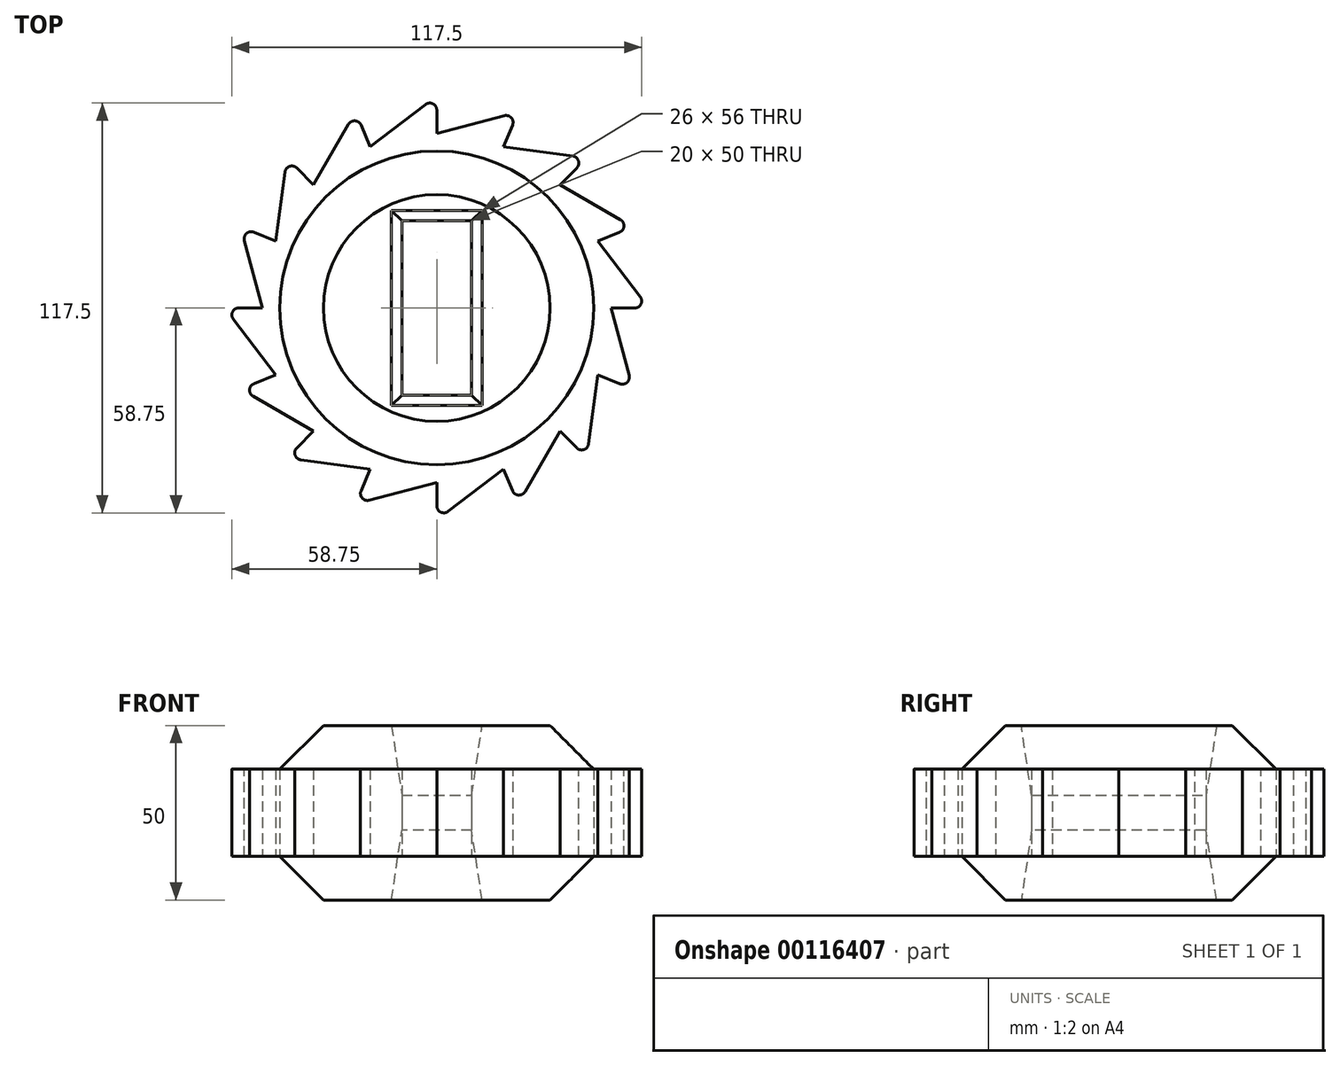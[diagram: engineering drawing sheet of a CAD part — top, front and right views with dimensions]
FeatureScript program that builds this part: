
annotation { "Feature Type Name" : "Feature", "Feature Type Description" : "" }
export const myFeature = defineFeature(function(context is Context, id is Id, definition is map)
    precondition{}
    {
        {
            var Q0;
            Q0=qCreatedBy(makeId("Top.planeOp"),FACE);
            var sketch = newSketch(context, id + "F0", { "sketchPlane" : qUnion([Q0])});
            skCircle(sketch, "E0.cCircle", {"center": v(0, 0) * mm, "radius": 50 * mm, "construction": true});
            skLineSegment(sketch, "E0.0", {"start": v(50, 0) * mm, "end": v(46.2, -19.13) * mm});
            skLineSegment(sketch, "E0.1", {"start": v(46.2, -19.13) * mm, "end": v(35.36, -35.36) * mm});
            skLineSegment(sketch, "E0.2", {"start": v(35.36, -35.36) * mm, "end": v(19.13, -46.2) * mm});
            skLineSegment(sketch, "E0.3", {"start": v(19.13, -46.2) * mm, "end": v(0, -50) * mm});
            skLineSegment(sketch, "E0.4", {"start": v(0, -50) * mm, "end": v(-19.13, -46.2) * mm});
            skLineSegment(sketch, "E0.5", {"start": v(-19.13, -46.2) * mm, "end": v(-35.36, -35.36) * mm});
            skLineSegment(sketch, "E0.6", {"start": v(-35.36, -35.36) * mm, "end": v(-46.2, -19.13) * mm});
            skLineSegment(sketch, "E0.7", {"start": v(-46.2, -19.13) * mm, "end": v(-50, 0) * mm});
            skLineSegment(sketch, "E0.8", {"start": v(-50, 0) * mm, "end": v(-46.2, 19.13) * mm});
            skLineSegment(sketch, "E0.9", {"start": v(-46.2, 19.13) * mm, "end": v(-35.36, 35.36) * mm});
            skLineSegment(sketch, "E0.10", {"start": v(-35.36, 35.36) * mm, "end": v(-19.13, 46.2) * mm});
            skLineSegment(sketch, "E0.11", {"start": v(-19.13, 46.2) * mm, "end": v(0, 50) * mm});
            skLineSegment(sketch, "E0.12", {"start": v(0, 50) * mm, "end": v(19.13, 46.2) * mm});
            skLineSegment(sketch, "E0.13", {"start": v(19.13, 46.2) * mm, "end": v(35.36, 35.36) * mm});
            skLineSegment(sketch, "E0.14", {"start": v(35.36, 35.36) * mm, "end": v(46.2, 19.13) * mm});
            skLineSegment(sketch, "E0.15", {"start": v(46.2, 19.13) * mm, "end": v(50, 0) * mm});
            skLineSegment(sketch, "E1", {"start": v(0, 60.8) * mm, "end": v(0, 50) * mm});
            skLineSegment(sketch, "E2", {"start": v(0, 60.8) * mm, "end": v(-19.13, 46.2) * mm});
            skLineSegment(sketch, "E3.1.0", {"start": v(-23.27, 56.17) * mm, "end": v(-35.36, 35.36) * mm});
            skLineSegment(sketch, "E3.1.1", {"start": v(-23.27, 56.17) * mm, "end": v(-19.13, 46.2) * mm});
            skLineSegment(sketch, "E3.2.0", {"start": v(-42.99, 42.99) * mm, "end": v(-46.2, 19.13) * mm});
            skLineSegment(sketch, "E3.2.1", {"start": v(-42.99, 42.99) * mm, "end": v(-35.36, 35.36) * mm});
            skLineSegment(sketch, "E3.3.0", {"start": v(-56.17, 23.27) * mm, "end": v(-50, 0) * mm});
            skLineSegment(sketch, "E3.3.1", {"start": v(-56.17, 23.27) * mm, "end": v(-46.2, 19.13) * mm});
            skLineSegment(sketch, "E3.4.0", {"start": v(-60.8, 0) * mm, "end": v(-46.2, -19.13) * mm});
            skLineSegment(sketch, "E3.4.1", {"start": v(-60.8, 0) * mm, "end": v(-50, 0) * mm});
            skLineSegment(sketch, "E3.5.0", {"start": v(-56.17, -23.27) * mm, "end": v(-35.36, -35.36) * mm});
            skLineSegment(sketch, "E3.5.1", {"start": v(-56.17, -23.27) * mm, "end": v(-46.2, -19.13) * mm});
            skLineSegment(sketch, "E3.6.0", {"start": v(-42.99, -42.99) * mm, "end": v(-19.13, -46.2) * mm});
            skLineSegment(sketch, "E3.6.1", {"start": v(-42.99, -42.99) * mm, "end": v(-35.36, -35.36) * mm});
            skLineSegment(sketch, "E3.7.0", {"start": v(-23.27, -56.17) * mm, "end": v(0, -50) * mm});
            skLineSegment(sketch, "E3.7.1", {"start": v(-23.27, -56.17) * mm, "end": v(-19.13, -46.2) * mm});
            skLineSegment(sketch, "E3.8.0", {"start": v(0, -60.8) * mm, "end": v(19.13, -46.2) * mm});
            skLineSegment(sketch, "E3.8.1", {"start": v(0, -60.8) * mm, "end": v(0, -50) * mm});
            skLineSegment(sketch, "E3.9.0", {"start": v(23.27, -56.17) * mm, "end": v(35.36, -35.36) * mm});
            skLineSegment(sketch, "E3.9.1", {"start": v(23.27, -56.17) * mm, "end": v(19.13, -46.2) * mm});
            skLineSegment(sketch, "E3.10.0", {"start": v(42.99, -42.99) * mm, "end": v(46.2, -19.13) * mm});
            skLineSegment(sketch, "E3.10.1", {"start": v(42.99, -42.99) * mm, "end": v(35.36, -35.36) * mm});
            skLineSegment(sketch, "E3.11.0", {"start": v(56.17, -23.27) * mm, "end": v(50, 0) * mm});
            skLineSegment(sketch, "E3.11.1", {"start": v(56.17, -23.27) * mm, "end": v(46.2, -19.13) * mm});
            skLineSegment(sketch, "E3.12.0", {"start": v(60.8, 0) * mm, "end": v(46.2, 19.13) * mm});
            skLineSegment(sketch, "E3.12.1", {"start": v(60.8, 0) * mm, "end": v(50, 0) * mm});
            skLineSegment(sketch, "E3.13.0", {"start": v(56.17, 23.27) * mm, "end": v(35.36, 35.36) * mm});
            skLineSegment(sketch, "E3.13.1", {"start": v(56.17, 23.27) * mm, "end": v(46.2, 19.13) * mm});
            skLineSegment(sketch, "E3.14.0", {"start": v(42.99, 42.99) * mm, "end": v(19.13, 46.2) * mm});
            skLineSegment(sketch, "E3.14.1", {"start": v(42.99, 42.99) * mm, "end": v(35.36, 35.36) * mm});
            skLineSegment(sketch, "E3.15.0", {"start": v(23.27, 56.17) * mm, "end": v(0, 50) * mm});
            skLineSegment(sketch, "E3.15.1", {"start": v(23.27, 56.17) * mm, "end": v(19.13, 46.2) * mm});
            skLineSegment(sketch, "E4.bottom", {"start": v(10, -25) * mm, "end": v(-10, -25) * mm});
            skLineSegment(sketch, "E4.top", {"start": v(10, 25) * mm, "end": v(-10, 25) * mm});
            skLineSegment(sketch, "E4.left", {"start": v(10, -25) * mm, "end": v(10, 25) * mm});
            skLineSegment(sketch, "E4.right", {"start": v(-10, -25) * mm, "end": v(-10, 25) * mm});
            skCircle(sketch, "E5", {"center": v(0, 0) * mm, "radius": 45 * mm});
            skSolve(sketch);
        }
        {
            var Q0;
            Q0=makeQuery(id+"F0.imprint","IMPRINT",FACE,{"disambiguationData":[TD([[makeQuery(id+"F0.imprint","IMPRINT",EDGE,{"derivedFrom":sQuery(id+"F0.wireOp",EDGE,"E0.0")}),-1.0]])]});
            var Q1;
            Q1=makeQuery(id+"F0.imprint","IMPRINT",FACE,{"disambiguationData":[TD([[makeQuery(id+"F0.imprint","IMPRINT",EDGE,{"derivedFrom":sQuery(id+"F0.wireOp",EDGE,"E4.bottom")}),1.0]])]});
            var Q2;
            Q2=makeQuery(id+"F0.imprint","IMPRINT",FACE,{"disambiguationData":[TD([[makeQuery(id+"F0.imprint","IMPRINT",EDGE,{"derivedFrom":sQuery(id+"F0.wireOp",EDGE,"E0.11")}),1.0]])]});
            var Q3;
            Q3=makeQuery(id+"F0.imprint","IMPRINT",FACE,{"disambiguationData":[TD([[makeQuery(id+"F0.imprint","IMPRINT",EDGE,{"derivedFrom":sQuery(id+"F0.wireOp",EDGE,"E0.10")}),1.0]])]});
            var Q4;
            Q4=makeQuery(id+"F0.imprint","IMPRINT",FACE,{"disambiguationData":[TD([[makeQuery(id+"F0.imprint","IMPRINT",EDGE,{"derivedFrom":sQuery(id+"F0.wireOp",EDGE,"E0.9")}),1.0]])]});
            var Q5;
            Q5=makeQuery(id+"F0.imprint","IMPRINT",FACE,{"disambiguationData":[TD([[makeQuery(id+"F0.imprint","IMPRINT",EDGE,{"derivedFrom":sQuery(id+"F0.wireOp",EDGE,"E0.8")}),1.0]])]});
            var Q6;
            Q6=makeQuery(id+"F0.imprint","IMPRINT",FACE,{"disambiguationData":[TD([[makeQuery(id+"F0.imprint","IMPRINT",EDGE,{"derivedFrom":sQuery(id+"F0.wireOp",EDGE,"E0.7")}),1.0]])]});
            var Q7;
            Q7=makeQuery(id+"F0.imprint","IMPRINT",FACE,{"disambiguationData":[TD([[makeQuery(id+"F0.imprint","IMPRINT",EDGE,{"derivedFrom":sQuery(id+"F0.wireOp",EDGE,"E0.6")}),1.0]])]});
            var Q8;
            Q8=makeQuery(id+"F0.imprint","IMPRINT",FACE,{"disambiguationData":[TD([[makeQuery(id+"F0.imprint","IMPRINT",EDGE,{"derivedFrom":sQuery(id+"F0.wireOp",EDGE,"E0.5")}),1.0]])]});
            var Q9;
            Q9=makeQuery(id+"F0.imprint","IMPRINT",FACE,{"disambiguationData":[TD([[makeQuery(id+"F0.imprint","IMPRINT",EDGE,{"derivedFrom":sQuery(id+"F0.wireOp",EDGE,"E0.4")}),1.0]])]});
            var Q10;
            Q10=makeQuery(id+"F0.imprint","IMPRINT",FACE,{"disambiguationData":[TD([[makeQuery(id+"F0.imprint","IMPRINT",EDGE,{"derivedFrom":sQuery(id+"F0.wireOp",EDGE,"E0.3")}),1.0]])]});
            var Q11;
            Q11=makeQuery(id+"F0.imprint","IMPRINT",FACE,{"disambiguationData":[TD([[makeQuery(id+"F0.imprint","IMPRINT",EDGE,{"derivedFrom":sQuery(id+"F0.wireOp",EDGE,"E0.2")}),1.0]])]});
            var Q12;
            Q12=makeQuery(id+"F0.imprint","IMPRINT",FACE,{"disambiguationData":[TD([[makeQuery(id+"F0.imprint","IMPRINT",EDGE,{"derivedFrom":sQuery(id+"F0.wireOp",EDGE,"E0.1")}),1.0]])]});
            var Q13;
            Q13=makeQuery(id+"F0.imprint","IMPRINT",FACE,{"disambiguationData":[TD([[makeQuery(id+"F0.imprint","IMPRINT",EDGE,{"derivedFrom":sQuery(id+"F0.wireOp",EDGE,"E0.0")}),1.0]])]});
            var Q14;
            Q14=makeQuery(id+"F0.imprint","IMPRINT",FACE,{"disambiguationData":[TD([[makeQuery(id+"F0.imprint","IMPRINT",EDGE,{"derivedFrom":sQuery(id+"F0.wireOp",EDGE,"E0.15")}),1.0]])]});
            var Q15;
            Q15=makeQuery(id+"F0.imprint","IMPRINT",FACE,{"disambiguationData":[TD([[makeQuery(id+"F0.imprint","IMPRINT",EDGE,{"derivedFrom":sQuery(id+"F0.wireOp",EDGE,"E0.14")}),1.0]])]});
            var Q16;
            Q16=makeQuery(id+"F0.imprint","IMPRINT",FACE,{"disambiguationData":[TD([[makeQuery(id+"F0.imprint","IMPRINT",EDGE,{"derivedFrom":sQuery(id+"F0.wireOp",EDGE,"E0.13")}),1.0]])]});
            var Q17;
            Q17=makeQuery(id+"F0.imprint","IMPRINT",FACE,{"disambiguationData":[TD([[makeQuery(id+"F0.imprint","IMPRINT",EDGE,{"derivedFrom":sQuery(id+"F0.wireOp",EDGE,"E0.12")}),1.0]])]});
            extrude(context, id + "F1", {"entities" : qUnion([Q0, Q1, Q2, Q3, Q4, Q5, Q6, Q7, Q8, Q9, Q10, Q11, Q12, Q13, Q14, Q15, Q16, Q17]), "endBound" : BoundingType.SYMMETRIC, "depth" : 25 * mm});
        }
        {
            var Q0;
            Q0=makeQuery(id+"F0.imprint","IMPRINT",FACE,{"disambiguationData":[TD([[makeQuery(id+"F0.imprint","IMPRINT",EDGE,{"derivedFrom":sQuery(id+"F0.wireOp",EDGE,"E4.bottom")}),1.0]])]});
            extrude(context, id + "F2", {"entities" : qUnion([Q0]), "endBound" : BoundingType.SYMMETRIC, "depth" : 50 * mm});
        }
        {
            var Q0;
            Q0=makeQuery(id+"F2.opExtrude","CAP_EDGE",EDGE,{"disambiguationData":[OSD([sQuery(id+"F0.wireOp",EDGE,"E5")])],"isStart":false});
            chamfer(context, id + "F3", {"entities" : qUnion([Q0]), "chamferType" : ChamferType.TWO_OFFSETS, "width1" : 12.5 * mm, "oppositeDirection" : false, "width2" : 12.5 * mm, "tangentPropagation" : true});
        }
        {
            var Q0;
            Q0=makeQuery(id+"F2.opExtrude","CAP_EDGE",EDGE,{"disambiguationData":[OSD([sQuery(id+"F0.wireOp",EDGE,"E5")])],"isStart":true});
            chamfer(context, id + "F4", {"entities" : qUnion([Q0]), "width" : 12.5 * mm, "tangentPropagation" : true});
        }
        {
            var Q0;
            Q0=makeQuery(id+"F1.opExtrude","SWEPT_EDGE",EDGE,{"disambiguationData":[OSD([sQuery(id+"F0.wireOp",EDGE,"E3.15.0"),sQuery(id+"F0.wireOp",EDGE,"E3.15.1")])]});
            var Q1;
            Q1=makeQuery(id+"F1.opExtrude","SWEPT_EDGE",EDGE,{"disambiguationData":[OSD([sQuery(id+"F0.wireOp",EDGE,"E1"),sQuery(id+"F0.wireOp",EDGE,"E2")])]});
            var Q2;
            Q2=makeQuery(id+"F1.opExtrude","SWEPT_EDGE",EDGE,{"disambiguationData":[OSD([sQuery(id+"F0.wireOp",EDGE,"E3.1.0"),sQuery(id+"F0.wireOp",EDGE,"E3.1.1")])]});
            var Q3;
            Q3=makeQuery(id+"F1.opExtrude","SWEPT_EDGE",EDGE,{"disambiguationData":[OSD([sQuery(id+"F0.wireOp",EDGE,"E3.2.0"),sQuery(id+"F0.wireOp",EDGE,"E3.2.1")])]});
            var Q4;
            Q4=makeQuery(id+"F1.opExtrude","SWEPT_EDGE",EDGE,{"disambiguationData":[OSD([sQuery(id+"F0.wireOp",EDGE,"E3.3.0"),sQuery(id+"F0.wireOp",EDGE,"E3.3.1")])]});
            var Q5;
            Q5=makeQuery(id+"F1.opExtrude","SWEPT_EDGE",EDGE,{"disambiguationData":[OSD([sQuery(id+"F0.wireOp",EDGE,"E3.4.0"),sQuery(id+"F0.wireOp",EDGE,"E3.4.1")])]});
            var Q6;
            Q6=makeQuery(id+"F1.opExtrude","SWEPT_EDGE",EDGE,{"disambiguationData":[OSD([sQuery(id+"F0.wireOp",EDGE,"E3.5.0"),sQuery(id+"F0.wireOp",EDGE,"E3.5.1")])]});
            var Q7;
            Q7=makeQuery(id+"F1.opExtrude","SWEPT_EDGE",EDGE,{"disambiguationData":[OSD([sQuery(id+"F0.wireOp",EDGE,"E3.6.0"),sQuery(id+"F0.wireOp",EDGE,"E3.6.1")])]});
            var Q8;
            Q8=makeQuery(id+"F1.opExtrude","SWEPT_EDGE",EDGE,{"disambiguationData":[OSD([sQuery(id+"F0.wireOp",EDGE,"E3.7.0"),sQuery(id+"F0.wireOp",EDGE,"E3.7.1")])]});
            var Q9;
            Q9=makeQuery(id+"F1.opExtrude","SWEPT_EDGE",EDGE,{"disambiguationData":[OSD([sQuery(id+"F0.wireOp",EDGE,"E3.8.0"),sQuery(id+"F0.wireOp",EDGE,"E3.8.1")])]});
            var Q10;
            Q10=makeQuery(id+"F1.opExtrude","SWEPT_EDGE",EDGE,{"disambiguationData":[OSD([sQuery(id+"F0.wireOp",EDGE,"E3.9.0"),sQuery(id+"F0.wireOp",EDGE,"E3.9.1")])]});
            var Q11;
            Q11=makeQuery(id+"F1.opExtrude","SWEPT_EDGE",EDGE,{"disambiguationData":[OSD([sQuery(id+"F0.wireOp",EDGE,"E3.14.0"),sQuery(id+"F0.wireOp",EDGE,"E3.14.1")])]});
            var Q12;
            Q12=makeQuery(id+"F1.opExtrude","SWEPT_EDGE",EDGE,{"disambiguationData":[OSD([sQuery(id+"F0.wireOp",EDGE,"E3.13.0"),sQuery(id+"F0.wireOp",EDGE,"E3.13.1")])]});
            var Q13;
            Q13=makeQuery(id+"F1.opExtrude","SWEPT_EDGE",EDGE,{"disambiguationData":[OSD([sQuery(id+"F0.wireOp",EDGE,"E3.12.0"),sQuery(id+"F0.wireOp",EDGE,"E3.12.1")])]});
            var Q14;
            Q14=makeQuery(id+"F1.opExtrude","SWEPT_EDGE",EDGE,{"disambiguationData":[OSD([sQuery(id+"F0.wireOp",EDGE,"E3.11.0"),sQuery(id+"F0.wireOp",EDGE,"E3.11.1")])]});
            var Q15;
            Q15=makeQuery(id+"F1.opExtrude","SWEPT_EDGE",EDGE,{"disambiguationData":[OSD([sQuery(id+"F0.wireOp",EDGE,"E3.10.0"),sQuery(id+"F0.wireOp",EDGE,"E3.10.1")])]});
            fillet(context, id + "F5", {"entities" : qUnion([Q0, Q1, Q2, Q3, Q4, Q5, Q6, Q7, Q8, Q9, Q10, Q11, Q12, Q13, Q14, Q15]), "radius" : 2 * mm, "tangentPropagation" : true, "allowEdgeOverflow" : false});
        }
        {
            var Q0;
            Q0=makeQuery(id+"F2.opExtrude","CAP_EDGE",EDGE,{"disambiguationData":[OSD([sQuery(id+"F0.wireOp",EDGE,"E4.top")])],"isStart":true});
            var Q1;
            Q1=makeQuery(id+"F2.opExtrude","CAP_EDGE",EDGE,{"disambiguationData":[OSD([sQuery(id+"F0.wireOp",EDGE,"E4.right")])],"isStart":true});
            var Q2;
            Q2=makeQuery(id+"F2.opExtrude","CAP_EDGE",EDGE,{"disambiguationData":[OSD([sQuery(id+"F0.wireOp",EDGE,"E4.left")])],"isStart":true});
            var Q3;
            Q3=makeQuery(id+"F2.opExtrude","CAP_EDGE",EDGE,{"disambiguationData":[OSD([sQuery(id+"F0.wireOp",EDGE,"E4.bottom")])],"isStart":true});
            var Q4;
            Q4=makeQuery(id+"F2.opExtrude","CAP_EDGE",EDGE,{"disambiguationData":[OSD([sQuery(id+"F0.wireOp",EDGE,"E4.right")])],"isStart":false});
            var Q5;
            Q5=makeQuery(id+"F2.opExtrude","CAP_EDGE",EDGE,{"disambiguationData":[OSD([sQuery(id+"F0.wireOp",EDGE,"E4.bottom")])],"isStart":false});
            var Q6;
            Q6=makeQuery(id+"F2.opExtrude","CAP_EDGE",EDGE,{"disambiguationData":[OSD([sQuery(id+"F0.wireOp",EDGE,"E4.top")])],"isStart":false});
            chamfer(context, id + "F6", {"entities" : qUnion([Q0, Q1, Q2, Q3, Q4, Q5, Q6]), "chamferType" : ChamferType.TWO_OFFSETS, "width1" : 3 * mm, "oppositeDirection" : false, "width2" : 20 * mm, "tangentPropagation" : true});
        }
        {
            var Q0;
            Q0=makeQuery(id+"F2.opExtrude","CAP_EDGE",EDGE,{"disambiguationData":[OSD([sQuery(id+"F0.wireOp",EDGE,"E4.left")])],"isStart":false});
            chamfer(context, id + "F7", {"entities" : qUnion([Q0]), "chamferType" : ChamferType.TWO_OFFSETS, "width1" : 20 * mm, "oppositeDirection" : false, "width2" : 3 * mm, "tangentPropagation" : true});
        }
    });
